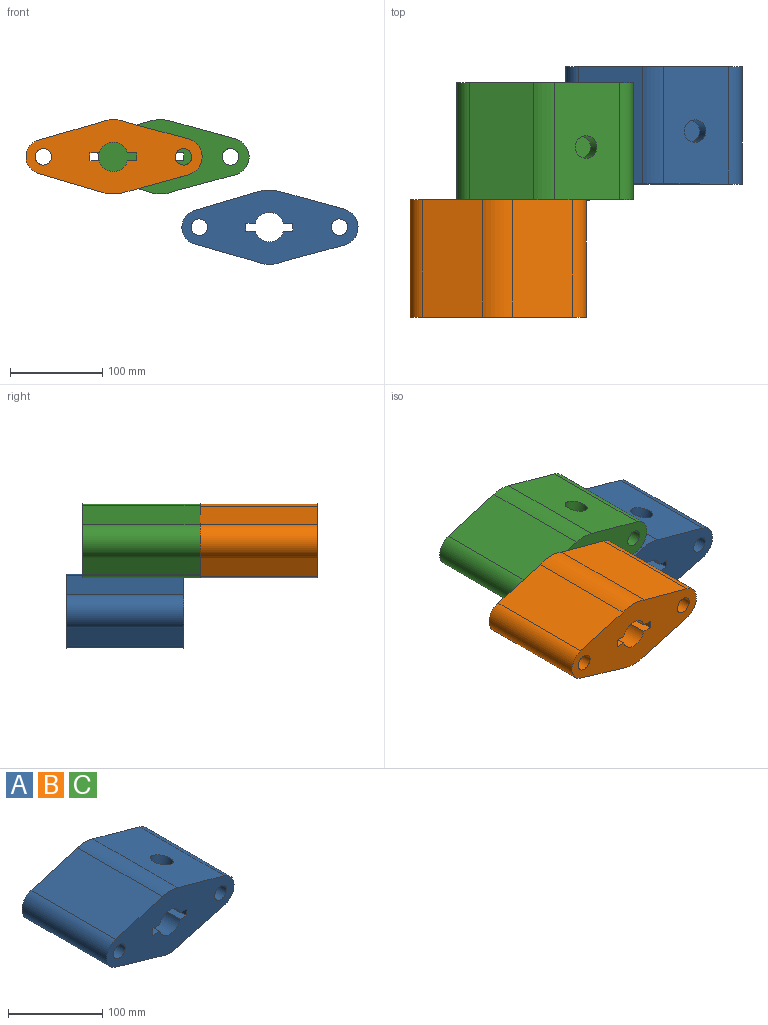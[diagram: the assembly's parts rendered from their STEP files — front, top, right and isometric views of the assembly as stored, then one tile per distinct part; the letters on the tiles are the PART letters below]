
ASSEMBLY  parts=3 mates=1
PART A: 22 faces, bbox 191x127x80.7 mm
  f0: cylinder r=15.88mm len=127mm, axis (0,1,0), area 5225mm2, adj f1,f17,f18,f19
  f1: plane 127x10.16mm, normal (0,0,1), area 1290.4mm2, adj f0,f2,f18,f19
  f2: plane 127x8.64mm, normal (1,0,0), area 1097.4mm2, adj f1,f3,f18,f19
  f3: plane 127x10.16mm, normal (0,0,-1), area 1290.4mm2, adj f2,f4,f18,f19
  f4: cylinder r=15.88mm len=127mm, axis (0,1,0), area 5225mm2, adj f3,f5,f18,f19
  f5: plane 127x10.16mm, normal (0,0,-1), area 1290.4mm2, adj f4,f6,f18,f19
  f6: plane 127x8.64mm, normal (-1,0,0), area 1097.4mm2, adj f5,f17,f18,f19
  f7: cylinder r=40.34mm len=127mm, axis (0,1,0), area 2936.4mm2, adj f8,f16,f18,f19
  f8: plane 127x69.94mm, normal (-0.28,0,0.96), area 9259.5mm2, adj f7,f9,f18,f19
  f9: cylinder r=18.85mm len=127mm, axis (0,1,0), area 6161.5mm2, adj f8,f10,f18,f19
  f10: plane 127x64.79mm, normal (-0.28,0,-0.96), area 8565.5mm2, adj f9,f11,f18,f19
  f11: cylinder r=40.34mm len=127mm, axis (0,1,0), area 4303.2mm2, adj f10,f12,f18,f19
  f12: plane 127x64.65mm, normal (0.26,0,-0.97), area 8500.9mm2, adj f11,f13,f18,f19
  f13: cylinder r=20.14mm len=127mm, axis (0,1,0), area 6693.7mm2, adj f12,f16,f18,f19
  f14: cylinder r=8.95mm len=127mm, axis (0,1,0), area 7138.1mm2, adj f18,f19
  f15: cylinder r=8.96mm len=127mm, axis (0,1,0), area 7147.2mm2, adj f18,f19
  f16: plane 127x69.96mm, normal (0.27,0,0.96), area 8747.2mm2, adj f7,f13,f18,f19,f20
  f17: plane 127x10.16mm, normal (0,0,1), area 1290.4mm2, adj f0,f6,f18,f19
  f18: plane 191.01x80.68mm, normal (0,-1,0), area 9141.2mm2, adj f0,f1,f2,f3,f4,f5,f6,f7
  f19: plane 191.01x80.68mm, normal (0,1,0), area 9141.2mm2, adj f0,f1,f2,f3,f4,f5,f6,f7
  f20: cylinder r=12.21mm len=30.98mm, axis (0.27,0,0.96), area 1948.8mm2, adj f16,f21
  f21: plane 24.42x23.54mm, normal (0.27,0,0.96), area 468.4mm2, adj f20
PART B: same geometry as A
PART C: same geometry as A
PLACE A t=(-2.85,41.1,-31.69)mm
PLACE B rot(axis=(1,0,0),180deg) t=(-171.91,-230.29,44.58)mm
PLACE C t=(-121.03,23.71,44.58)mm
MATE planar B.f18 <-> C.f18  axis (0,1,0) through (-146.47,-103.29,48.9)mm
